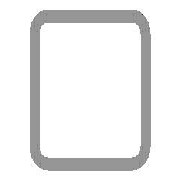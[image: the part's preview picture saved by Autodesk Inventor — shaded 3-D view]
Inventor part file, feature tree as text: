
AUTODESK INVENTOR PART (.ipt)
format: ipt  version: 2025.3 (Build 293356030, 356C)  size: 135,168 bytes
history: native  units: mm (DEFAULTED — no unit token found)
features: other x4, sketch x1, plane x1
ambient origin geometry x8: Origin, YZ Plane, XZ Plane, XY Plane, X Axis, Y Axis, Z Axis, Center Point
bodies: Solid1 (feature_tree), Body (feature_tree)
feature tree (6):
  parser-record x1  (decoder bookkeeping rows leaked as tree rows — omitted from the tree; the rows remain in map.json)
  other  "Driven Length"
  other  "Start Plane"
  other  "End Plane"
  sketch  "Sketch3"  dims[d3=570.0mm d4=0.0mm d7=4.0mm d9=40.0mm d11=40.0mm d12=2.0mm d13=40.0mm d14=610.0mm d15=20.0mm d16=20.0mm d17=90.0deg d18=570.0mm]
  plane  "Work Plane3"
